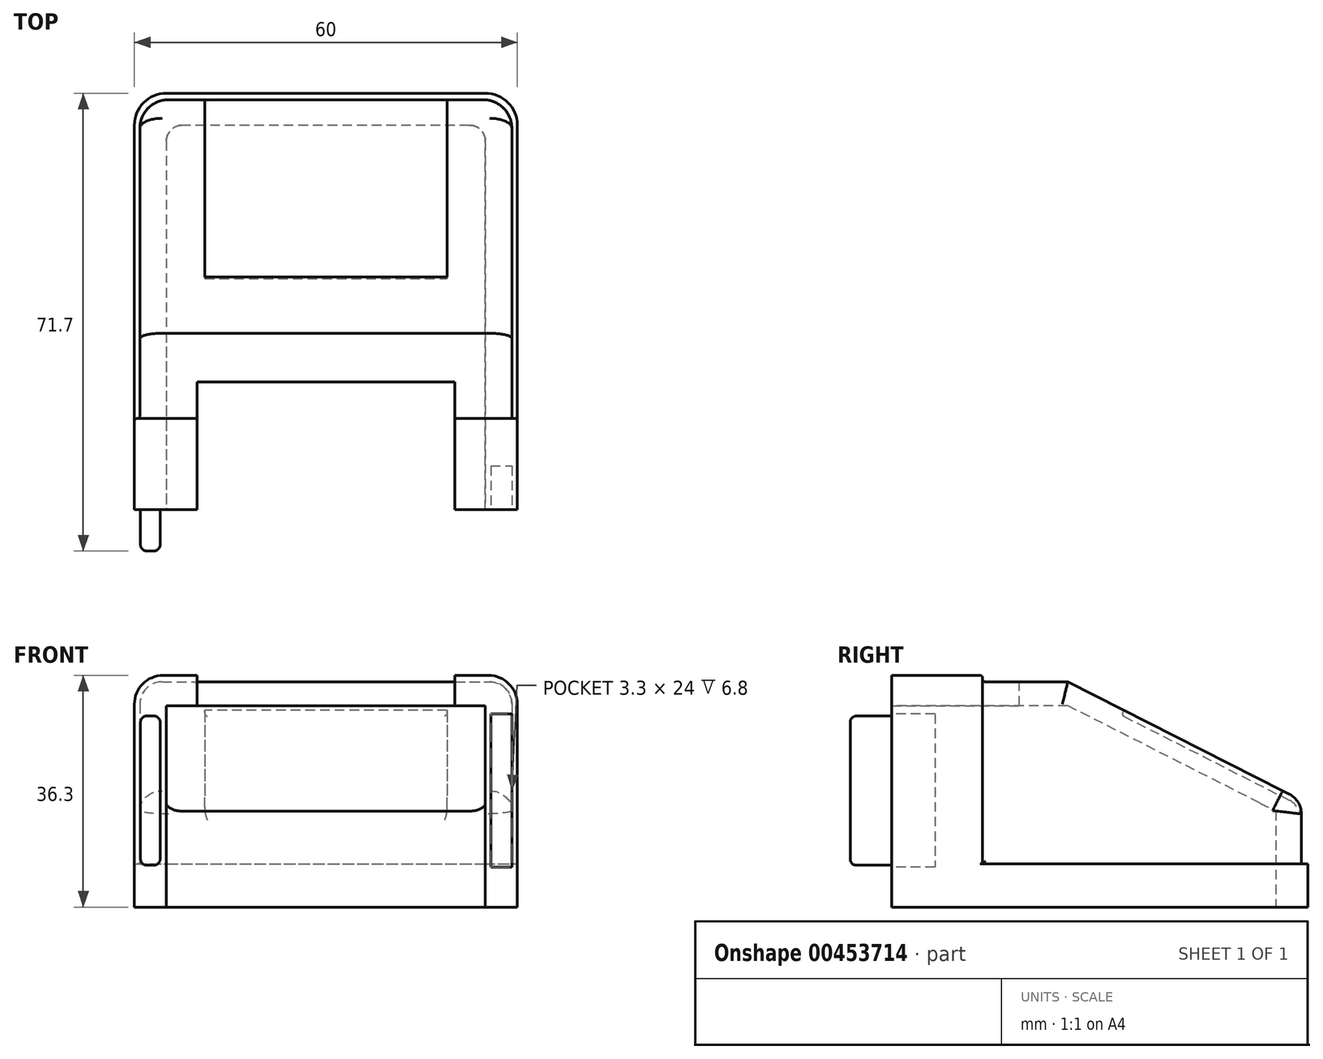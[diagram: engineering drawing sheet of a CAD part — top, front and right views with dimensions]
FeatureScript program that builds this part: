
annotation { "Feature Type Name" : "Feature", "Feature Type Description" : "" }
export const myFeature = defineFeature(function(context is Context, id is Id, definition is map)
    precondition{}
    {
        {
            var Q0;
            Q0=qCreatedBy(makeId("Top.planeOp"),FACE);
            var sketch = newSketch(context, id + "F0", { "sketchPlane" : qUnion([Q0])});
            skLineSegment(sketch, "E0.bottom", {"start": v(-25, 27.6) * mm, "end": v(0, 27.6) * mm});
            skLineSegment(sketch, "E0.top", {"start": v(-30, -37.6) * mm, "end": v(-25, -37.6) * mm});
            skLineSegment(sketch, "E0.left", {"start": v(-30, 22.6) * mm, "end": v(-30, -37.6) * mm});
            skLineSegment(sketch, "E0.right", {"start": v(0, 27.6) * mm, "end": v(0, 22.6) * mm});
            skLineSegment(sketch, "E1.bottom", {"start": v(-22.5, 22.6) * mm, "end": v(0, 22.6) * mm});
            skLineSegment(sketch, "E1.left", {"start": v(-25, 20.1) * mm, "end": v(-25, -37.6) * mm});
            skPoint(sketch, "E2.orphan", {"position": v(0, -37.6) * mm});
            skPoint(sketch, "E3.visualSharp", {"position": v(-30, 27.6) * mm});
            skArc(sketch, "E3.filletArc", {"start": v(-25, 27.6) * mm, "mid": v(-28.54, 26.14) * mm, "end": v(-30, 22.6) * mm});
            skArc(sketch, "E4.filletArc", {"start": v(-22.5, 22.6) * mm, "mid": v(-24.27, 21.88) * mm, "end": v(-25, 20.1) * mm});
            skLineSegment(sketch, "E5.MirrorCS", {"start": v(22.5, 22.6) * mm, "end": v(0, 22.6) * mm});
            skArc(sketch, "E6.MirrorCS", {"start": v(22.5, 22.6) * mm, "mid": v(24.27, 21.88) * mm, "end": v(25, 20.1) * mm});
            skLineSegment(sketch, "E7.MirrorCS", {"start": v(25, 20.1) * mm, "end": v(25, -37.6) * mm});
            skLineSegment(sketch, "E8.MirrorCS", {"start": v(30, -37.6) * mm, "end": v(25, -37.6) * mm});
            skLineSegment(sketch, "E9.MirrorCS", {"start": v(30, 22.6) * mm, "end": v(30, -37.6) * mm});
            skArc(sketch, "E10.MirrorCS", {"start": v(25, 27.6) * mm, "mid": v(28.54, 26.14) * mm, "end": v(30, 22.6) * mm});
            skLineSegment(sketch, "E11.MirrorCS", {"start": v(25, 27.6) * mm, "end": v(0, 27.6) * mm});
            skSolve(sketch);
        }
        {
            var Q0;
            Q0 = qSketchRegion(id + "F0", true);
            extrude(context, id + "F1", {"entities" : qUnion([Q0]), "depth" : 36.3 * mm});
        }
        {
            var Q0;
            Q0=makeQuery(id+"F1.opExtrude","SWEPT_FACE",FACE,{"disambiguationData":[OSD([sQuery(id+"F0.wireOp",EDGE,"E9.MirrorCS")])]});
            var sketch = newSketch(context, id + "F2", { "sketchPlane" : qUnion([Q0])});
            skLineSegment(sketch, "E12", {"start": v(-23.34, 36.3) * mm, "end": v(-23.34, 35.3) * mm});
            skLineSegment(sketch, "E13", {"start": v(-23.34, 35.3) * mm, "end": v(-10, 35.3) * mm});
            skLineSegment(sketch, "E14", {"start": v(-10, 35.3) * mm, "end": v(26.6, 16.75) * mm});
            skLineSegment(sketch, "E15", {"start": v(27.6, 16.24) * mm, "end": v(27.6, 6.75) * mm});
            skLineSegment(sketch, "E16", {"start": v(27.6, 6.75) * mm, "end": v(27.6, 36.3) * mm});
            skLineSegment(sketch, "E17", {"start": v(27.6, 36.3) * mm, "end": v(-23.34, 36.3) * mm});
            skLineSegment(sketch, "E18", {"start": v(26.6, 16.75) * mm, "end": v(26.6, 6.75) * mm});
            skLineSegment(sketch, "E19", {"start": v(26.6, 6.75) * mm, "end": v(27.6, 6.75) * mm});
            skPoint(sketch, "E20.orphan", {"position": v(27.6, 0) * mm});
            skSolve(sketch);
        }
        {
            var Q0;
            Q0 = qSketchRegion(id + "F2", true);
            var Q1;
            Q1=makeQuery(id+"F1.opExtrude","SWEPT_FACE",FACE,{"disambiguationData":[OSD([sQuery(id+"F0.wireOp",EDGE,"E0.left")])]});
            extrude(context, id + "F3", {"entities" : qUnion([Q0]), "operationType" : NewBodyOperationType.REMOVE, "endBound" : BoundingType.UP_TO_SURFACE, "oppositeDirection" : true, "endBoundEntityFace" : qUnion([Q1]), "depth" : 25 * mm});
        }
        {
            var Q0;
            Q0=makeQuery(id+"F1.opExtrude","SWEPT_FACE",FACE,{"disambiguationData":[OSD([sQuery(id+"F0.wireOp",EDGE,"E7.MirrorCS")])]});
            var sketch = newSketch(context, id + "F4", { "sketchPlane" : qUnion([Q0])});
            skLineSegment(sketch, "E21", {"start": v(37.6, 31.56) * mm, "end": v(10, 31.56) * mm});
            skLineSegment(sketch, "E22", {"start": v(10, 31.56) * mm, "end": v(-23.6, 14.53) * mm});
            skLineSegment(sketch, "E23", {"start": v(-23.6, 14.53) * mm, "end": v(-23.6, 0) * mm});
            skLineSegment(sketch, "E24", {"start": v(-23.6, 0) * mm, "end": v(-27.6, 0) * mm});
            skLineSegment(sketch, "E25", {"start": v(-27.6, 0) * mm, "end": v(-27.6, 6.75) * mm});
            skLineSegment(sketch, "E26", {"start": v(-27.6, 6.75) * mm, "end": v(-26.6, 6.75) * mm});
            skLineSegment(sketch, "E27", {"start": v(-26.6, 6.75) * mm, "end": v(-26.6, 16.75) * mm});
            skLineSegment(sketch, "E28", {"start": v(-26.6, 16.75) * mm, "end": v(10, 35.3) * mm});
            skLineSegment(sketch, "E29", {"start": v(10, 35.3) * mm, "end": v(16.65, 35.3) * mm});
            skLineSegment(sketch, "E30", {"start": v(16.65, 35.3) * mm, "end": v(23.34, 35.3) * mm});
            skLineSegment(sketch, "E31", {"start": v(23.34, 35.3) * mm, "end": v(23.34, 36.3) * mm});
            skLineSegment(sketch, "E32", {"start": v(23.34, 36.3) * mm, "end": v(37.6, 36.3) * mm});
            skLineSegment(sketch, "E33", {"start": v(37.6, 36.3) * mm, "end": v(37.6, 31.56) * mm});
            skSolve(sketch);
        }
        {
            var Q0;
            Q0 = qSketchRegion(id + "F4", true);
            var Q1;
            Q1=makeQuery(id+"F1.opExtrude","SWEPT_FACE",FACE,{"disambiguationData":[OSD([sQuery(id+"F0.wireOp",EDGE,"E1.left")])]});
            extrude(context, id + "F5", {"entities" : qUnion([Q0]), "operationType" : NewBodyOperationType.ADD, "endBound" : BoundingType.UP_TO_SURFACE, "endBoundEntityFace" : qUnion([Q1]), "depth" : 25 * mm});
        }
        {
            var Q0;
            {var subQ0=sQuery(id+"F0.wireOp",EDGE,"E7.MirrorCS");var subQ1=sQuery(id+"F0.wireOp",EDGE,"E8.MirrorCS");var subQ2=sQuery(id+"F0.wireOp",EDGE,"E9.MirrorCS");var subQ4=sQuery(id+"F0.wireOp",EDGE,"E1.left");var subQ5=sQuery(id+"F0.wireOp",EDGE,"E0.left");var subQ6=sQuery(id+"F0.wireOp",EDGE,"E0.top");var subQ7=makeQuery(id+"F1.opExtrude","CAP_FACE",FACE,{"disambiguationData":[OSD([sQuery(id+"F0.wireOp",EDGE,"E0.bottom"),subQ6,subQ5,sQuery(id+"F0.wireOp",EDGE,"E1.bottom"),subQ4,sQuery(id+"F0.wireOp",EDGE,"E3.filletArc"),sQuery(id+"F0.wireOp",EDGE,"E4.filletArc"),sQuery(id+"F0.wireOp",EDGE,"E5.MirrorCS"),sQuery(id+"F0.wireOp",EDGE,"E6.MirrorCS"),subQ0,subQ1,subQ2,sQuery(id+"F0.wireOp",EDGE,"E10.MirrorCS"),sQuery(id+"F0.wireOp",EDGE,"E11.MirrorCS")])],"isStart":false});Q0=makeQuery(id+"F5.boolean.opBoolean","MERGE",FACE,{"derivedFrom":[makeQuery(id+"F3.boolean.opBoolean","SPLIT",FACE,{"disambiguationData":[TD([makeQuery(id+"F1.opExtrude","SWEPT_FACE",FACE,{"disambiguationData":[OSD([subQ6])]})])],"derivedFrom":subQ7}),makeQuery(id+"F3.boolean.opBoolean","SPLIT",FACE,{"disambiguationData":[TD([makeQuery(id+"F1.opExtrude","SWEPT_FACE",FACE,{"disambiguationData":[OSD([subQ0])]})])],"derivedFrom":subQ7}),makeQuery(id+"F5.opExtrude","SWEPT_FACE",FACE,{"disambiguationData":[OSD([sQuery(id+"F4.wireOp",EDGE,"E32")])]})]});}
            var sketch = newSketch(context, id + "F6", { "sketchPlane" : qUnion([Q0])});
            skLineSegment(sketch, "E34.bottom", {"start": v(-20.2, -37.6) * mm, "end": v(20.2, -37.6) * mm});
            skLineSegment(sketch, "E34.top", {"start": v(-20.2, -17.6) * mm, "end": v(20.2, -17.6) * mm});
            skLineSegment(sketch, "E34.left", {"start": v(-20.2, -37.6) * mm, "end": v(-20.2, -17.6) * mm});
            skLineSegment(sketch, "E34.right", {"start": v(20.2, -37.6) * mm, "end": v(20.2, -17.6) * mm});
            skPoint(sketch, "E35", {"position": v(0, -37.6) * mm});
            skSolve(sketch);
        }
        {
            var Q0;
            Q0 = qSketchRegion(id + "F6", true);
            var Q1;
            Q1=makeQuery(id+"F5.opExtrude","SWEPT_FACE",FACE,{"disambiguationData":[OSD([sQuery(id+"F4.wireOp",EDGE,"E21")])]});
            extrude(context, id + "F7", {"entities" : qUnion([Q0]), "operationType" : NewBodyOperationType.REMOVE, "endBound" : BoundingType.UP_TO_SURFACE, "oppositeDirection" : true, "endBoundEntityFace" : qUnion([Q1]), "depth" : 25 * mm});
        }
        {
            var Q0;
            Q0=makeQuery(id+"F5.boolean.opBoolean","MERGE",FACE,{"derivedFrom":[makeQuery(id+"F3.boolean.opBoolean","COPY",FACE,{"derivedFrom":makeQuery(id+"F3.opExtrude","SWEPT_FACE",FACE,{"disambiguationData":[OSD([sQuery(id+"F2.wireOp",EDGE,"E14")])]})}),makeQuery(id+"F5.opExtrude","SWEPT_FACE",FACE,{"disambiguationData":[OSD([sQuery(id+"F4.wireOp",EDGE,"E28")])]})]});
            var sketch = newSketch(context, id + "F8", { "sketchPlane" : qUnion([Q0])});
            skLineSegment(sketch, "E36.bottom", {"start": v(19, -14.99) * mm, "end": v(-19, -14.99) * mm});
            skLineSegment(sketch, "E36.top", {"start": v(19, 16.16) * mm, "end": v(-19, 16.16) * mm});
            skLineSegment(sketch, "E36.left", {"start": v(19, -14.99) * mm, "end": v(19, 16.16) * mm});
            skLineSegment(sketch, "E36.right", {"start": v(-19, -14.99) * mm, "end": v(-19, 16.16) * mm});
            skPoint(sketch, "E37", {"position": v(0, -14.99) * mm});
            skLineSegment(sketch, "E38.bottom", {"start": v(-19, 16.16) * mm, "end": v(19, 16.16) * mm});
            skLineSegment(sketch, "E38.top", {"start": v(-19, 19.64) * mm, "end": v(19, 19.64) * mm});
            skLineSegment(sketch, "E38.left", {"start": v(-19, 16.16) * mm, "end": v(-19, 19.64) * mm});
            skLineSegment(sketch, "E38.right", {"start": v(19, 16.16) * mm, "end": v(19, 19.64) * mm});
            skLineSegment(sketch, "E39.bottom", {"start": v(19, 16.16) * mm, "end": v(19, 16.16) * mm});
            skLineSegment(sketch, "E39.top", {"start": v(19, 16.16) * mm, "end": v(19, 16.16) * mm});
            skLineSegment(sketch, "E39.left", {"start": v(19, 16.16) * mm, "end": v(19, 16.16) * mm});
            skLineSegment(sketch, "E39.right", {"start": v(19, 16.16) * mm, "end": v(19, 16.16) * mm});
            skSolve(sketch);
        }
        {
            var Q0;
            Q0 = qSketchRegion(id + "F8", true);
            extrude(context, id + "F9", {"entities" : qUnion([Q0]), "operationType" : NewBodyOperationType.REMOVE, "oppositeDirection" : true, "depth" : 0.85 * mm});
        }
        {
            var Q0;
            Q0=makeQuery(id+"F3.boolean.opBoolean","COPY",FACE,{"derivedFrom":makeQuery(id+"F3.opExtrude","SWEPT_FACE",FACE,{"disambiguationData":[OSD([sQuery(id+"F2.wireOp",EDGE,"E19")])]})});
            var sketch = newSketch(context, id + "F10", { "sketchPlane" : qUnion([Q0])});
            skLineSegment(sketch, "E40", {"start": v(-30, -23.34) * mm, "end": v(-29.15, -23.34) * mm});
            skLineSegment(sketch, "E41", {"start": v(-29.15, -23.34) * mm, "end": v(-29.15, 22.1) * mm});
            skLineSegment(sketch, "E42", {"start": v(-24.65, 26.6) * mm, "end": v(0, 26.6) * mm});
            skPoint(sketch, "E42.endSnap0", {"position": v(0, 26.6) * mm});
            skLineSegment(sketch, "E43", {"start": v(0, 26.6) * mm, "end": v(0, 27.6) * mm});
            skLineSegment(sketch, "E44", {"start": v(0, 27.6) * mm, "end": v(-30, 27.6) * mm});
            skLineSegment(sketch, "E45", {"start": v(-30, 27.6) * mm, "end": v(-30, -23.34) * mm});
            skLineSegment(sketch, "E46", {"start": v(0, 26.6) * mm, "end": v(0, -55.24) * mm, "construction": true});
            skLineSegment(sketch, "E47.MirrorCS", {"start": v(30, 27.6) * mm, "end": v(30, -23.34) * mm});
            skLineSegment(sketch, "E48.MirrorCS", {"start": v(0, 27.6) * mm, "end": v(30, 27.6) * mm});
            skLineSegment(sketch, "E49.MirrorCS", {"start": v(24.65, 26.6) * mm, "end": v(0, 26.6) * mm});
            skLineSegment(sketch, "E50.MirrorCS", {"start": v(29.15, -23.34) * mm, "end": v(29.15, 22.1) * mm});
            skLineSegment(sketch, "E51.MirrorCS", {"start": v(30, -23.34) * mm, "end": v(29.15, -23.34) * mm});
            skPoint(sketch, "E52.visualSharp", {"position": v(-29.15, 26.6) * mm});
            skArc(sketch, "E52.filletArc", {"start": v(-24.65, 26.6) * mm, "mid": v(-27.83, 25.3) * mm, "end": v(-29.15, 22.1) * mm});
            skArc(sketch, "E53.MirrorCS", {"start": v(24.65, 26.6) * mm, "mid": v(27.83, 25.3) * mm, "end": v(29.15, 22.1) * mm});
            skPoint(sketch, "E54.orphan", {"position": v(29.15, 26.6) * mm});
            skSolve(sketch);
        }
        {
            var Q0;
            Q0 = qSketchRegion(id + "F10", true);
            var Q1;
            {var subQ0=sQuery(id+"F0.wireOp",EDGE,"E8.MirrorCS");var subQ2=sQuery(id+"F0.wireOp",EDGE,"E9.MirrorCS");var subQ3=sQuery(id+"F0.wireOp",EDGE,"E7.MirrorCS");var subQ4=sQuery(id+"F0.wireOp",EDGE,"E1.left");var subQ5=sQuery(id+"F0.wireOp",EDGE,"E0.left");var subQ6=sQuery(id+"F0.wireOp",EDGE,"E0.top");var subQ7=makeQuery(id+"F1.opExtrude","CAP_FACE",FACE,{"disambiguationData":[OSD([sQuery(id+"F0.wireOp",EDGE,"E0.bottom"),subQ6,subQ5,sQuery(id+"F0.wireOp",EDGE,"E1.bottom"),subQ4,sQuery(id+"F0.wireOp",EDGE,"E3.filletArc"),sQuery(id+"F0.wireOp",EDGE,"E4.filletArc"),sQuery(id+"F0.wireOp",EDGE,"E5.MirrorCS"),sQuery(id+"F0.wireOp",EDGE,"E6.MirrorCS"),subQ3,subQ0,subQ2,sQuery(id+"F0.wireOp",EDGE,"E10.MirrorCS"),sQuery(id+"F0.wireOp",EDGE,"E11.MirrorCS")])],"isStart":false});var subQ10=makeQuery(id+"F1.opExtrude","SWEPT_FACE",FACE,{"disambiguationData":[OSD([subQ5])]});var subQ12=makeQuery(id+"F1.opExtrude","SWEPT_FACE",FACE,{"disambiguationData":[OSD([subQ6])]});var subQ13=makeQuery(id+"F1.opExtrude","SWEPT_FACE",FACE,{"disambiguationData":[OSD([subQ3])]});Q1=makeQuery(id+"F7.boolean.opBoolean","SPLIT",FACE,{"disambiguationData":[TD([subQ10])],"derivedFrom":makeQuery(id+"F5.boolean.opBoolean","MERGE",FACE,{"derivedFrom":[makeQuery(id+"F3.boolean.opBoolean","SPLIT",FACE,{"disambiguationData":[TD([subQ12])],"derivedFrom":subQ7}),makeQuery(id+"F3.boolean.opBoolean","SPLIT",FACE,{"disambiguationData":[TD([subQ13])],"derivedFrom":subQ7}),makeQuery(id+"F5.opExtrude","SWEPT_FACE",FACE,{"disambiguationData":[OSD([sQuery(id+"F4.wireOp",EDGE,"E32")])]})]})});}
            extrude(context, id + "F11", {"entities" : qUnion([Q0]), "operationType" : NewBodyOperationType.REMOVE, "endBound" : BoundingType.UP_TO_SURFACE, "endBoundEntityFace" : qUnion([Q1]), "depth" : 25 * mm});
        }
        {
            var Q0;
            Q0=makeQuery(id+"F9.boolean.opBoolean","INTERSECT",EDGE,{"derivedFrom":[makeQuery(id+"F3.boolean.opBoolean","COPY",FACE,{"derivedFrom":makeQuery(id+"F3.opExtrude","SWEPT_FACE",FACE,{"disambiguationData":[OSD([sQuery(id+"F2.wireOp",EDGE,"E18")])]})}),makeQuery(id+"F9.opExtrude","CAP_FACE",FACE,{"disambiguationData":[OSD([sQuery(id+"F8.wireOp",EDGE,"E36.bottom"),sQuery(id+"F8.wireOp",EDGE,"E36.left"),sQuery(id+"F8.wireOp",EDGE,"E36.right"),sQuery(id+"F8.wireOp",EDGE,"E38.top"),sQuery(id+"F8.wireOp",EDGE,"E38.left"),sQuery(id+"F8.wireOp",EDGE,"E38.right")])],"isStart":false})]});
            fillet(context, id + "F12", {"entities" : qUnion([Q0]), "radius" : 3.5 * mm, "tangentPropagation" : true, "allowEdgeOverflow" : false});
        }
        {
            var Q0;
            {var subQ2=makeQuery(id+"F3.opExtrude","SWEPT_FACE",FACE,{"disambiguationData":[OSD([sQuery(id+"F2.wireOp",EDGE,"E13")])]});Q0=makeQuery(id+"F11.boolean.opBoolean","INTERSECT",EDGE,{"derivedFrom":[makeQuery(id+"F5.boolean.opBoolean","MERGE",FACE,{"derivedFrom":[makeQuery(id+"F3.boolean.opBoolean","COPY",FACE,{"disambiguationData":[TD([makeQuery(id+"F1.opExtrude","SWEPT_FACE",FACE,{"disambiguationData":[OSD([sQuery(id+"F0.wireOp",EDGE,"E0.left")])]})])],"derivedFrom":subQ2}),makeQuery(id+"F3.boolean.opBoolean","COPY",FACE,{"disambiguationData":[TD([makeQuery(id+"F1.opExtrude","SWEPT_FACE",FACE,{"disambiguationData":[OSD([sQuery(id+"F0.wireOp",EDGE,"E7.MirrorCS")])]})])],"derivedFrom":subQ2}),makeQuery(id+"F5.opExtrude","SWEPT_FACE",FACE,{"disambiguationData":[OSD([sQuery(id+"F4.wireOp",EDGE,"E29"),sQuery(id+"F4.wireOp",EDGE,"E30")])]})]}),makeQuery(id+"F11.opExtrude","SWEPT_FACE",FACE,{"disambiguationData":[OSD([sQuery(id+"F10.wireOp",EDGE,"E50.MirrorCS")])]})]});}
            var Q1;
            {var subQ2=makeQuery(id+"F3.opExtrude","SWEPT_FACE",FACE,{"disambiguationData":[OSD([sQuery(id+"F2.wireOp",EDGE,"E13")])]});Q1=makeQuery(id+"F11.boolean.opBoolean","INTERSECT",EDGE,{"derivedFrom":[makeQuery(id+"F5.boolean.opBoolean","MERGE",FACE,{"derivedFrom":[makeQuery(id+"F3.boolean.opBoolean","COPY",FACE,{"disambiguationData":[TD([makeQuery(id+"F1.opExtrude","SWEPT_FACE",FACE,{"disambiguationData":[OSD([sQuery(id+"F0.wireOp",EDGE,"E0.left")])]})])],"derivedFrom":subQ2}),makeQuery(id+"F3.boolean.opBoolean","COPY",FACE,{"disambiguationData":[TD([makeQuery(id+"F1.opExtrude","SWEPT_FACE",FACE,{"disambiguationData":[OSD([sQuery(id+"F0.wireOp",EDGE,"E7.MirrorCS")])]})])],"derivedFrom":subQ2}),makeQuery(id+"F5.opExtrude","SWEPT_FACE",FACE,{"disambiguationData":[OSD([sQuery(id+"F4.wireOp",EDGE,"E29"),sQuery(id+"F4.wireOp",EDGE,"E30")])]})]}),makeQuery(id+"F11.opExtrude","SWEPT_FACE",FACE,{"disambiguationData":[OSD([sQuery(id+"F10.wireOp",EDGE,"E41")])]})]});}
            var Q2;
            Q2=makeQuery(id+"F11.boolean.opBoolean","INTERSECT",EDGE,{"derivedFrom":[makeQuery(id+"F5.boolean.opBoolean","MERGE",FACE,{"derivedFrom":[makeQuery(id+"F3.boolean.opBoolean","COPY",FACE,{"derivedFrom":makeQuery(id+"F3.opExtrude","SWEPT_FACE",FACE,{"disambiguationData":[OSD([sQuery(id+"F2.wireOp",EDGE,"E14")])]})}),makeQuery(id+"F5.opExtrude","SWEPT_FACE",FACE,{"disambiguationData":[OSD([sQuery(id+"F4.wireOp",EDGE,"E28")])]})]}),makeQuery(id+"F11.opExtrude","SWEPT_FACE",FACE,{"disambiguationData":[OSD([sQuery(id+"F10.wireOp",EDGE,"E50.MirrorCS")])]})]});
            var Q3;
            Q3=makeQuery(id+"F11.boolean.opBoolean","INTERSECT",EDGE,{"derivedFrom":[makeQuery(id+"F5.boolean.opBoolean","MERGE",FACE,{"derivedFrom":[makeQuery(id+"F3.boolean.opBoolean","COPY",FACE,{"derivedFrom":makeQuery(id+"F3.opExtrude","SWEPT_FACE",FACE,{"disambiguationData":[OSD([sQuery(id+"F2.wireOp",EDGE,"E14")])]})}),makeQuery(id+"F5.opExtrude","SWEPT_FACE",FACE,{"disambiguationData":[OSD([sQuery(id+"F4.wireOp",EDGE,"E28")])]})]}),makeQuery(id+"F11.opExtrude","SWEPT_FACE",FACE,{"disambiguationData":[OSD([sQuery(id+"F10.wireOp",EDGE,"E41")])]})]});
            var Q4;
            {var subQ0=sQuery(id+"F2.wireOp",EDGE,"E18");var subQ1=sQuery(id+"F2.wireOp",EDGE,"E14");Q4=makeQuery(id+"F9.boolean.opBoolean","SPLIT",EDGE,{"disambiguationData":[TD([makeQuery(id+"F1.opExtrude","SWEPT_FACE",FACE,{"disambiguationData":[OSD([sQuery(id+"F0.wireOp",EDGE,"E10.MirrorCS")])]})])],"derivedFrom":makeQuery(id+"F3.boolean.opBoolean","COPY",EDGE,{"derivedFrom":makeQuery(id+"F3.opExtrude","SWEPT_EDGE",EDGE,{"disambiguationData":[OSD([subQ1,subQ0])]})})});}
            var Q5;
            {var subQ0=sQuery(id+"F2.wireOp",EDGE,"E18");var subQ1=sQuery(id+"F2.wireOp",EDGE,"E14");Q5=makeQuery(id+"F9.boolean.opBoolean","SPLIT",EDGE,{"disambiguationData":[TD([makeQuery(id+"F1.opExtrude","SWEPT_FACE",FACE,{"disambiguationData":[OSD([sQuery(id+"F0.wireOp",EDGE,"E3.filletArc")])]})])],"derivedFrom":makeQuery(id+"F3.boolean.opBoolean","COPY",EDGE,{"derivedFrom":makeQuery(id+"F3.opExtrude","SWEPT_EDGE",EDGE,{"disambiguationData":[OSD([subQ1,subQ0])]})})});}
            fillet(context, id + "F13", {"entities" : qUnion([Q0, Q1, Q2, Q3, Q4, Q5]), "radius" : 3.5 * mm, "allowEdgeOverflow" : false});
        }
        {
            var Q0;
            Q0=makeQuery(id+"F1.opExtrude","CAP_EDGE",EDGE,{"disambiguationData":[OSD([sQuery(id+"F0.wireOp",EDGE,"E0.left")])],"isStart":false});
            var Q1;
            Q1=makeQuery(id+"F1.opExtrude","CAP_EDGE",EDGE,{"disambiguationData":[OSD([sQuery(id+"F0.wireOp",EDGE,"E9.MirrorCS")])],"isStart":false});
            fillet(context, id + "F14", {"entities" : qUnion([Q0, Q1]), "radius" : 4.5 * mm, "tangentPropagation" : true, "allowEdgeOverflow" : false});
        }
        {
            var Q0;
            Q0=makeQuery(id+"F9.boolean.opBoolean","COPY",EDGE,{"derivedFrom":makeQuery(id+"F9.opExtrude","CAP_EDGE",EDGE,{"disambiguationData":[OSD([sQuery(id+"F8.wireOp",EDGE,"E36.bottom")])],"isStart":false})});
            var Q1;
            Q1=makeQuery(id+"F9.boolean.opBoolean","COPY",EDGE,{"derivedFrom":makeQuery(id+"F9.opExtrude","CAP_EDGE",EDGE,{"disambiguationData":[OSD([sQuery(id+"F8.wireOp",EDGE,"E36.left")])],"isStart":false})});
            var Q2;
            Q2=makeQuery(id+"F9.boolean.opBoolean","COPY",EDGE,{"derivedFrom":makeQuery(id+"F9.opExtrude","CAP_EDGE",EDGE,{"disambiguationData":[OSD([sQuery(id+"F8.wireOp",EDGE,"E36.right")])],"isStart":false})});
            var Q3;
            Q3=makeQuery(id+"F9.boolean.opBoolean","COPY",EDGE,{"derivedFrom":makeQuery(id+"F9.opExtrude","CAP_EDGE",EDGE,{"disambiguationData":[OSD([sQuery(id+"F8.wireOp",EDGE,"E36.bottom")])],"isStart":true})});
            var Q4;
            Q4=makeQuery(id+"F9.boolean.opBoolean","COPY",EDGE,{"derivedFrom":makeQuery(id+"F9.opExtrude","CAP_EDGE",EDGE,{"disambiguationData":[OSD([sQuery(id+"F8.wireOp",EDGE,"E36.right")])],"isStart":true})});
            var Q5;
            Q5=makeQuery(id+"F9.boolean.opBoolean","COPY",EDGE,{"derivedFrom":makeQuery(id+"F9.opExtrude","CAP_EDGE",EDGE,{"disambiguationData":[OSD([sQuery(id+"F8.wireOp",EDGE,"E36.left")])],"isStart":true})});
            var Q6;
            {var subQ0=sQuery(id+"F0.wireOp",EDGE,"E0.left");var subQ1=makeQuery(id+"F1.opExtrude","SWEPT_FACE",FACE,{"disambiguationData":[OSD([subQ0])]});var subQ2=sQuery(id+"F2.wireOp",EDGE,"E12");var subQ7=sQuery(id+"F2.wireOp",EDGE,"E13");var subQ9=sQuery(id+"F0.wireOp",EDGE,"E9.MirrorCS");var subQ10=sQuery(id+"F0.wireOp",EDGE,"E7.MirrorCS");var subQ12=makeQuery(id+"F1.opExtrude","SWEPT_FACE",FACE,{"disambiguationData":[OSD([subQ10])]});var subQ13=makeQuery(id+"F1.opExtrude","SWEPT_FACE",FACE,{"disambiguationData":[OSD([subQ9])]});var subQ14=sQuery(id+"F4.wireOp",EDGE,"E31");var subQ15=sQuery(id+"F4.wireOp",EDGE,"E30");var subQ16=makeQuery(id+"F3.opExtrude","SWEPT_EDGE",EDGE,{"disambiguationData":[OSD([subQ2,subQ7])]});Q6=makeQuery(id+"F7.boolean.opBoolean","SPLIT",EDGE,{"disambiguationData":[TD([subQ13])],"derivedFrom":makeQuery(id+"F5.boolean.opBoolean","MERGE",EDGE,{"derivedFrom":[makeQuery(id+"F3.boolean.opBoolean","COPY",EDGE,{"disambiguationData":[TD([subQ1])],"derivedFrom":subQ16}),makeQuery(id+"F3.boolean.opBoolean","COPY",EDGE,{"disambiguationData":[TD([subQ12])],"derivedFrom":subQ16}),makeQuery(id+"F5.opExtrude","SWEPT_EDGE",EDGE,{"disambiguationData":[OSD([subQ15,subQ14])]})]})});}
            var Q7;
            {var subQ0=sQuery(id+"F0.wireOp",EDGE,"E0.left");var subQ1=makeQuery(id+"F1.opExtrude","SWEPT_FACE",FACE,{"disambiguationData":[OSD([subQ0])]});var subQ2=sQuery(id+"F2.wireOp",EDGE,"E12");var subQ7=sQuery(id+"F2.wireOp",EDGE,"E13");var subQ10=sQuery(id+"F0.wireOp",EDGE,"E7.MirrorCS");var subQ12=makeQuery(id+"F1.opExtrude","SWEPT_FACE",FACE,{"disambiguationData":[OSD([subQ10])]});var subQ14=sQuery(id+"F4.wireOp",EDGE,"E31");var subQ15=sQuery(id+"F4.wireOp",EDGE,"E30");var subQ16=makeQuery(id+"F3.opExtrude","SWEPT_EDGE",EDGE,{"disambiguationData":[OSD([subQ2,subQ7])]});Q7=makeQuery(id+"F7.boolean.opBoolean","SPLIT",EDGE,{"disambiguationData":[TD([subQ1])],"derivedFrom":makeQuery(id+"F5.boolean.opBoolean","MERGE",EDGE,{"derivedFrom":[makeQuery(id+"F3.boolean.opBoolean","COPY",EDGE,{"disambiguationData":[TD([subQ1])],"derivedFrom":subQ16}),makeQuery(id+"F3.boolean.opBoolean","COPY",EDGE,{"disambiguationData":[TD([subQ12])],"derivedFrom":subQ16}),makeQuery(id+"F5.opExtrude","SWEPT_EDGE",EDGE,{"disambiguationData":[OSD([subQ15,subQ14])]})]})});}
            var Q8;
            {var subQ0=sQuery(id+"F0.wireOp",EDGE,"E9.MirrorCS");var subQ1=sQuery(id+"F0.wireOp",EDGE,"E7.MirrorCS");var subQ3=sQuery(id+"F0.wireOp",EDGE,"E0.left");var subQ6=makeQuery(id+"F1.opExtrude","SWEPT_FACE",FACE,{"disambiguationData":[OSD([subQ1])]});var subQ8=sQuery(id+"F2.wireOp",EDGE,"E12");var subQ10=sQuery(id+"F4.wireOp",EDGE,"E31");var subQ12=makeQuery(id+"F1.opExtrude","SWEPT_FACE",FACE,{"disambiguationData":[OSD([subQ3])]});var subQ13=sQuery(id+"F4.wireOp",EDGE,"E32");var subQ14=makeQuery(id+"F3.opExtrude","SWEPT_EDGE",EDGE,{"disambiguationData":[OSD([subQ0,subQ8,sQuery(id+"F2.wireOp",EDGE,"E17")])]});Q8=makeQuery(id+"F7.boolean.opBoolean","SPLIT",EDGE,{"disambiguationData":[TD([subQ12])],"derivedFrom":makeQuery(id+"F5.boolean.opBoolean","MERGE",EDGE,{"derivedFrom":[makeQuery(id+"F3.boolean.opBoolean","COPY",EDGE,{"disambiguationData":[TD([subQ12])],"derivedFrom":subQ14}),makeQuery(id+"F3.boolean.opBoolean","COPY",EDGE,{"disambiguationData":[TD([subQ6])],"derivedFrom":subQ14}),makeQuery(id+"F5.opExtrude","SWEPT_EDGE",EDGE,{"disambiguationData":[OSD([subQ10,subQ13])]})]})});}
            var Q9;
            {var subQ0=sQuery(id+"F0.wireOp",EDGE,"E9.MirrorCS");var subQ1=sQuery(id+"F0.wireOp",EDGE,"E7.MirrorCS");var subQ3=sQuery(id+"F0.wireOp",EDGE,"E0.left");var subQ6=makeQuery(id+"F1.opExtrude","SWEPT_FACE",FACE,{"disambiguationData":[OSD([subQ1])]});var subQ7=makeQuery(id+"F1.opExtrude","SWEPT_FACE",FACE,{"disambiguationData":[OSD([subQ0])]});var subQ8=sQuery(id+"F2.wireOp",EDGE,"E12");var subQ10=sQuery(id+"F4.wireOp",EDGE,"E31");var subQ12=makeQuery(id+"F1.opExtrude","SWEPT_FACE",FACE,{"disambiguationData":[OSD([subQ3])]});var subQ13=sQuery(id+"F4.wireOp",EDGE,"E32");var subQ14=makeQuery(id+"F3.opExtrude","SWEPT_EDGE",EDGE,{"disambiguationData":[OSD([subQ0,subQ8,sQuery(id+"F2.wireOp",EDGE,"E17")])]});Q9=makeQuery(id+"F7.boolean.opBoolean","SPLIT",EDGE,{"disambiguationData":[TD([subQ7])],"derivedFrom":makeQuery(id+"F5.boolean.opBoolean","MERGE",EDGE,{"derivedFrom":[makeQuery(id+"F3.boolean.opBoolean","COPY",EDGE,{"disambiguationData":[TD([subQ12])],"derivedFrom":subQ14}),makeQuery(id+"F3.boolean.opBoolean","COPY",EDGE,{"disambiguationData":[TD([subQ6])],"derivedFrom":subQ14}),makeQuery(id+"F5.opExtrude","SWEPT_EDGE",EDGE,{"disambiguationData":[OSD([subQ10,subQ13])]})]})});}
            var Q10;
            Q10=makeQuery(id+"F11.boolean.opBoolean","COPY",EDGE,{"derivedFrom":makeQuery(id+"F11.opExtrude","CAP_EDGE",EDGE,{"disambiguationData":[OSD([sQuery(id+"F10.wireOp",EDGE,"E41")])],"isStart":true})});
            var Q11;
            Q11=makeQuery(id+"F11.boolean.opBoolean","COPY",EDGE,{"derivedFrom":makeQuery(id+"F11.opExtrude","CAP_EDGE",EDGE,{"disambiguationData":[OSD([sQuery(id+"F10.wireOp",EDGE,"E45")])],"isStart":true})});
            fillet(context, id + "F15", {"entities" : qUnion([Q0, Q1, Q2, Q3, Q4, Q5, Q6, Q7, Q8, Q9, Q10, Q11]), "radius" : 0.4 * mm, "tangentPropagation" : true, "allowEdgeOverflow" : false});
        }
        {
            var Q0;
            {var subQ3=sQuery(id+"F0.wireOp",EDGE,"E8.MirrorCS");var subQ4=sQuery(id+"F0.wireOp",EDGE,"E7.MirrorCS");var subQ12=sQuery(id+"F0.wireOp",EDGE,"E0.top");Q0=makeQuery(id+"F7.boolean.opBoolean","SPLIT",FACE,{"disambiguationData":[TD([makeQuery(id+"F1.opExtrude","SWEPT_FACE",FACE,{"disambiguationData":[OSD([subQ4])]})])],"derivedFrom":makeQuery(id+"F5.boolean.opBoolean","MERGE",FACE,{"derivedFrom":[makeQuery(id+"F1.opExtrude","SWEPT_FACE",FACE,{"disambiguationData":[OSD([subQ12])]}),makeQuery(id+"F1.opExtrude","SWEPT_FACE",FACE,{"disambiguationData":[OSD([subQ3])]}),makeQuery(id+"F5.opExtrude","SWEPT_FACE",FACE,{"disambiguationData":[OSD([sQuery(id+"F4.wireOp",EDGE,"E33")])]})]})});}
            var sketch = newSketch(context, id + "F16", { "sketchPlane" : qUnion([Q0])});
            skLineSegment(sketch, "E55.bottom", {"start": v(25.85, 30.25) * mm, "end": v(29.15, 30.25) * mm});
            skLineSegment(sketch, "E55.top", {"start": v(25.85, 6.25) * mm, "end": v(29.15, 6.25) * mm});
            skLineSegment(sketch, "E55.left", {"start": v(25.85, 30.25) * mm, "end": v(25.85, 6.25) * mm});
            skLineSegment(sketch, "E55.right", {"start": v(29.15, 30.25) * mm, "end": v(29.15, 6.25) * mm});
            skLineSegment(sketch, "E56", {"start": v(30, 6.25) * mm, "end": v(25, 6.25) * mm, "construction": true});
            skPoint(sketch, "E57", {"position": v(27.5, 6.25) * mm});
            skSolve(sketch);
        }
        {
            var Q0;
            Q0 = qSketchRegion(id + "F16", true);
            extrude(context, id + "F17", {"entities" : qUnion([Q0]), "operationType" : NewBodyOperationType.REMOVE, "oppositeDirection" : true, "depth" : 6.8 * mm});
        }
        {
            var Q0;
            {var subQ0=sQuery(id+"F0.wireOp",EDGE,"E0.left");var subQ5=sQuery(id+"F0.wireOp",EDGE,"E8.MirrorCS");var subQ12=sQuery(id+"F0.wireOp",EDGE,"E0.top");Q0=makeQuery(id+"F7.boolean.opBoolean","SPLIT",FACE,{"disambiguationData":[TD([makeQuery(id+"F1.opExtrude","SWEPT_FACE",FACE,{"disambiguationData":[OSD([subQ0])]})])],"derivedFrom":makeQuery(id+"F5.boolean.opBoolean","MERGE",FACE,{"derivedFrom":[makeQuery(id+"F1.opExtrude","SWEPT_FACE",FACE,{"disambiguationData":[OSD([subQ12])]}),makeQuery(id+"F1.opExtrude","SWEPT_FACE",FACE,{"disambiguationData":[OSD([subQ5])]}),makeQuery(id+"F5.opExtrude","SWEPT_FACE",FACE,{"disambiguationData":[OSD([sQuery(id+"F4.wireOp",EDGE,"E33")])]})]})});}
            var sketch = newSketch(context, id + "F18", { "sketchPlane" : qUnion([Q0])});
            skLineSegment(sketch, "E58.bottom", {"start": v(-29.05, 29.95) * mm, "end": v(-25.95, 29.95) * mm});
            skLineSegment(sketch, "E58.top", {"start": v(-29.05, 6.55) * mm, "end": v(-25.95, 6.55) * mm});
            skLineSegment(sketch, "E58.left", {"start": v(-29.05, 29.95) * mm, "end": v(-29.05, 6.55) * mm});
            skLineSegment(sketch, "E58.right", {"start": v(-25.95, 29.95) * mm, "end": v(-25.95, 6.55) * mm});
            skLineSegment(sketch, "E59", {"start": v(26.91, 6.25) * mm, "end": v(-25, 6.25) * mm, "construction": true});
            skLineSegment(sketch, "E60", {"start": v(24.74, 30.25) * mm, "end": v(-25, 30.25) * mm, "construction": true});
            skLineSegment(sketch, "E61", {"start": v(-30, 8.37) * mm, "end": v(-25, 8.37) * mm, "construction": true});
            skPoint(sketch, "E62", {"position": v(-27.5, 8.37) * mm});
            skPoint(sketch, "E63", {"position": v(-27.5, 6.55) * mm});
            skLineSegment(sketch, "E64", {"start": v(-27.5, 8.37) * mm, "end": v(-27.5, 2.58) * mm, "construction": true});
            skSolve(sketch);
        }
        {
            var Q0;
            Q0 = qSketchRegion(id + "F18", true);
            extrude(context, id + "F19", {"entities" : qUnion([Q0]), "operationType" : NewBodyOperationType.ADD, "depth" : 6.5 * mm});
        }
        {
            var Q0;
            Q0=makeQuery(id+"F19.opExtrude","SWEPT_EDGE",EDGE,{"disambiguationData":[OSD([sQuery(id+"F18.wireOp",EDGE,"E58.bottom"),sQuery(id+"F18.wireOp",EDGE,"E58.left")])]});
            var Q1;
            Q1=makeQuery(id+"F19.opExtrude","SWEPT_EDGE",EDGE,{"disambiguationData":[OSD([sQuery(id+"F18.wireOp",EDGE,"E58.bottom"),sQuery(id+"F18.wireOp",EDGE,"E58.right")])]});
            var Q2;
            Q2=makeQuery(id+"F19.opExtrude","SWEPT_EDGE",EDGE,{"disambiguationData":[OSD([sQuery(id+"F18.wireOp",EDGE,"E58.top"),sQuery(id+"F18.wireOp",EDGE,"E58.left")])]});
            var Q3;
            Q3=makeQuery(id+"F19.opExtrude","SWEPT_EDGE",EDGE,{"disambiguationData":[OSD([sQuery(id+"F18.wireOp",EDGE,"E58.top"),sQuery(id+"F18.wireOp",EDGE,"E58.right")])]});
            var Q4;
            Q4=makeQuery(id+"F19.opExtrude","CAP_EDGE",EDGE,{"disambiguationData":[OSD([sQuery(id+"F18.wireOp",EDGE,"E58.left")])],"isStart":false});
            var Q5;
            Q5=makeQuery(id+"F19.opExtrude","CAP_EDGE",EDGE,{"disambiguationData":[OSD([sQuery(id+"F18.wireOp",EDGE,"E58.right")])],"isStart":false});
            var Q6;
            Q6=makeQuery(id+"F19.opExtrude","CAP_EDGE",EDGE,{"disambiguationData":[OSD([sQuery(id+"F18.wireOp",EDGE,"E58.top")])],"isStart":false});
            var Q7;
            Q7=makeQuery(id+"F19.opExtrude","CAP_EDGE",EDGE,{"disambiguationData":[OSD([sQuery(id+"F18.wireOp",EDGE,"E58.bottom")])],"isStart":false});
            fillet(context, id + "F20", {"entities" : qUnion([Q0, Q1, Q2, Q3, Q4, Q5, Q6, Q7]), "radius" : 1 * mm, "tangentPropagation" : true, "allowEdgeOverflow" : false});
        }
    });
